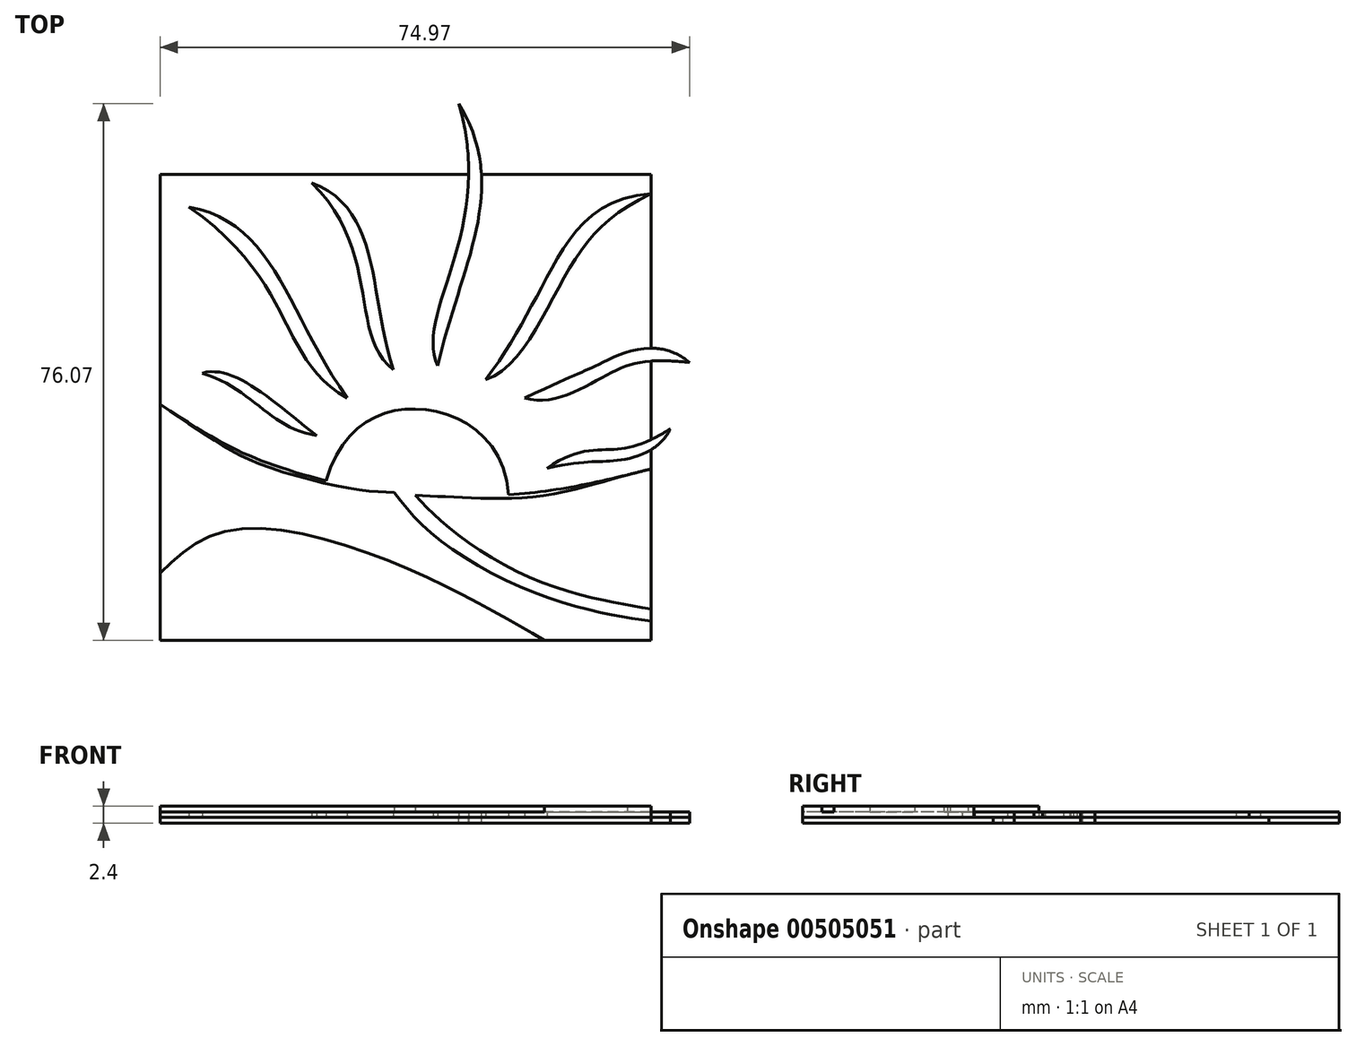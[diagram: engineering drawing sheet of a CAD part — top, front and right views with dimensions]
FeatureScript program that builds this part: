
annotation { "Feature Type Name" : "Feature", "Feature Type Description" : "" }
export const myFeature = defineFeature(function(context is Context, id is Id, definition is map)
    precondition{}
    {
        {
            var Q0;
            Q0=qCreatedBy(makeId("Top.planeOp"),FACE);
            var sketch = newSketch(context, id + "F0", { "sketchPlane" : qUnion([Q0])});
            skFitSpline(sketch, "E0", {"points": [v(7.74, 45.02) * mm, v(4.8, 7.87) * mm], "startDerivative": vector(22.58, -36) * mm, "endDerivative": vector(-9.15, -41.56) * mm});
            skFitSpline(sketch, "E1", {"points": [v(7.74, 45.02) * mm, v(4.8, 7.87) * mm], "startDerivative": vector(16.22, -53.48) * mm, "endDerivative": vector(10.7, -21.96) * mm});
            skFitSpline(sketch, "E2", {"points": [v(-13.07, 33.8) * mm, v(-1.52, 7.33) * mm], "startDerivative": vector(29.95, -11.67) * mm, "endDerivative": vector(10.67, -32.95) * mm});
            skFitSpline(sketch, "E3", {"points": [v(-13.07, 33.8) * mm, v(-1.52, 7.33) * mm], "startDerivative": vector(29.76, -29.08) * mm, "endDerivative": vector(19.1, -14.6) * mm});
            skFitSpline(sketch, "E4", {"points": [v(-30.44, 30.38) * mm, v(-8.06, 3.29) * mm], "startDerivative": vector(36.4, -6.71) * mm, "endDerivative": vector(26.15, -37.64) * mm});
            skFitSpline(sketch, "E5", {"points": [v(-30.44, 30.38) * mm, v(-8.06, 3.29) * mm], "startDerivative": vector(46.65, -33.04) * mm, "endDerivative": vector(30.4, -17.67) * mm});
            skFitSpline(sketch, "E6", {"points": [v(-28.55, 6.82) * mm, v(-12.38, -2.01) * mm], "startDerivative": vector(13.32, 3.79) * mm, "endDerivative": vector(19.77, -15.57) * mm});
            skFitSpline(sketch, "E7", {"points": [v(-28.55, 6.82) * mm, v(-12.38, -2.01) * mm], "startDerivative": vector(21.88, -6.87) * mm, "endDerivative": vector(19.77, -2.95) * mm});
            skFitSpline(sketch, "E8", {"points": [v(34.97, 32.25) * mm, v(20.43, 20.76) * mm, v(11.57, 5.91) * mm], "startDerivative": vector(-48.83, -2.88) * mm, "endDerivative": vector(-23.4, -30.3) * mm});
            skFitSpline(sketch, "E9", {"points": [v(34.97, 32.25) * mm, v(22.17, 19.45) * mm, v(11.57, 5.91) * mm], "startDerivative": vector(-41.02, -19.12) * mm, "endDerivative": vector(-28.23, -8.78) * mm});
            skFitSpline(sketch, "E10", {"points": [v(17.1, 3.33) * mm, v(27.54, 8.06) * mm, v(40.44, 8.34) * mm], "startDerivative": vector(45.36, 20.62) * mm, "endDerivative": vector(27.22, -23) * mm});
            skFitSpline(sketch, "E11", {"points": [v(17.1, 3.33) * mm, v(28.93, 6.67) * mm, v(40.44, 8.34) * mm], "startDerivative": vector(23.68, -8.22) * mm, "endDerivative": vector(37.55, -3.72) * mm});
            skFitSpline(sketch, "E12", {"points": [v(20.26, -6.67) * mm, v(29.5, -4) * mm, v(37.72, -1.06) * mm], "startDerivative": vector(23.46, 16.94) * mm, "endDerivative": vector(22.55, 14.35) * mm});
            skFitSpline(sketch, "E13", {"points": [v(20.26, -6.67) * mm, v(30.1, -5.56) * mm, v(37.72, -1.06) * mm], "startDerivative": vector(33.1, 7.46) * mm, "endDerivative": vector(9.27, 19.9) * mm});
            skFitSpline(sketch, "E14", {"points": [v(1.58, -10.48) * mm, v(16.98, -20.87) * mm, v(34.98, -26.6) * mm], "startDerivative": vector(27.12, -26.11) * mm, "endDerivative": vector(39.88, -7.31) * mm});
            skFitSpline(sketch, "E15", {"points": [v(-1.37, -10.12) * mm, v(16.48, -22.6) * mm, v(34.98, -28.32) * mm], "startDerivative": vector(30.47, -33.38) * mm, "endDerivative": vector(41.23, -6.87) * mm});
            skFitSpline(sketch, "E16", {"points": [v(1.58, -10.48) * mm, v(19.87, -9.92) * mm, v(34.98, -6.75) * mm], "startDerivative": vector(38.98, -1.92) * mm, "endDerivative": vector(30.53, 7.96) * mm});
            skFitSpline(sketch, "E17", {"points": [v(-34.53, -21.5) * mm, v(-7.42, -19.32) * mm, v(19.89, -31.05) * mm], "startDerivative": vector(55.55, 36.09) * mm, "endDerivative": vector(52.91, -30.06) * mm});
            skFitSpline(sketch, "E18", {"points": [v(-34.53, -23.76) * mm, v(-8.68, -20.91) * mm, v(16.38, -31.05) * mm], "startDerivative": vector(51.38, 35.5) * mm, "endDerivative": vector(49.5, -23.12) * mm});
            skFitSpline(sketch, "E19", {"points": [v(-34.53, 2.42) * mm, v(-18.75, -6.1) * mm, v(-1.37, -10.12) * mm], "startDerivative": vector(44.86, -30.13) * mm, "endDerivative": vector(37.4, -3.65) * mm});
            skFitSpline(sketch, "E20", {"points": [v(-11.02, -8.42) * mm, v(2.1, 1.72) * mm, v(14.8, -10.43) * mm], "startDerivative": vector(13.26, 46.27) * mm, "endDerivative": vector(3.47, -48.26) * mm});
            skLineSegment(sketch, "E21", {"start": v(-34.53, 35) * mm, "end": v(-34.53, -31.05) * mm});
            skLineSegment(sketch, "E22", {"start": v(-34.53, 35) * mm, "end": v(9.16, 35) * mm});
            skLineSegment(sketch, "E23", {"start": v(-34.53, -31.05) * mm, "end": v(34.98, -31.05) * mm});
            skLineSegment(sketch, "E24.trimOffspring", {"start": v(10.97, 35) * mm, "end": v(34.97, 35) * mm});
            skLineSegment(sketch, "E25", {"start": v(34.98, -31.05) * mm, "end": v(34.98, -4.04) * mm});
            skLineSegment(sketch, "E26.trimOffspring", {"start": v(34.98, 10.35) * mm, "end": v(34.97, 35) * mm});
            skLineSegment(sketch, "E27.trimOffspring", {"start": v(34.98, -2.6) * mm, "end": v(34.98, 8.53) * mm});
            skSolve(sketch);
        }
        {
            var Q0;
            Q0 = qSketchRegion(id + "F0", true);
            var Q1;
            Q1=makeQuery(id+"F0.imprint","IMPRINT",FACE,{"disambiguationData":[TD([[makeQuery(id+"F0.imprint","IMPRINT",EDGE,{"derivedFrom":sQuery(id+"F0.wireOp",EDGE,"E2")}),-1.0]])]});
            var Q2;
            Q2=makeQuery(id+"F0.imprint","IMPRINT",FACE,{"disambiguationData":[TD([[makeQuery(id+"F0.imprint","IMPRINT",EDGE,{"derivedFrom":sQuery(id+"F0.wireOp",EDGE,"E4")}),-1.0]])]});
            var Q3;
            Q3=makeQuery(id+"F0.imprint","IMPRINT",FACE,{"disambiguationData":[TD([[makeQuery(id+"F0.imprint","IMPRINT",EDGE,{"derivedFrom":sQuery(id+"F0.wireOp",EDGE,"E6")}),-1.0]])]});
            extrude(context, id + "F1", {"entities" : qUnion([Q0, Q1, Q2, Q3]), "oppositeDirection" : true, "depth" : .8 * mm});
        }
        {
            var Q0;
            Q0=makeQuery(id+"F0.imprint","IMPRINT",FACE,{"disambiguationData":[TD([[makeQuery(id+"F0.imprint","IMPRINT",EDGE,{"derivedFrom":sQuery(id+"F0.wireOp",EDGE,"E6")}),-1.0]])]});
            var Q1;
            Q1=makeQuery(id+"F0.imprint","IMPRINT",FACE,{"disambiguationData":[TD([[makeQuery(id+"F0.imprint","IMPRINT",EDGE,{"derivedFrom":sQuery(id+"F0.wireOp",EDGE,"E4")}),-1.0]])]});
            var Q2;
            Q2=makeQuery(id+"F0.imprint","IMPRINT",FACE,{"disambiguationData":[TD([[makeQuery(id+"F0.imprint","IMPRINT",EDGE,{"derivedFrom":sQuery(id+"F0.wireOp",EDGE,"E2")}),-1.0]])]});
            var Q3;
            Q3=makeQuery(id+"F0.imprint","IMPRINT",FACE,{"disambiguationData":[TD([[makeQuery(id+"F0.imprint","IMPRINT",EDGE,{"derivedFrom":sQuery(id+"F0.wireOp",EDGE,"E8")}),1.0]])]});
            var Q4;
            {var subQ0=sQuery(id+"F0.wireOp",EDGE,"E11");var subQ1=sQuery(id+"F0.wireOp",EDGE,"E10");var subQ2=makeQuery(id+"F0.imprint","INTERSECT",VERTEX,{"disambiguationData":[OD(0.0)],"derivedFrom":[subQ1,subQ0]});Q4=makeQuery(id+"F0.imprint","IMPRINT",FACE,{"disambiguationData":[TD([[makeQuery(id+"F0.imprint","IMPRINT",EDGE,{"disambiguationData":[TD([[subQ2,-1.0]])],"derivedFrom":subQ1}),-1.0]])]});}
            var Q5;
            {var subQ0=sQuery(id+"F0.wireOp",EDGE,"E1");var subQ1=sQuery(id+"F0.wireOp",EDGE,"E0");var subQ2=makeQuery(id+"F0.imprint","INTERSECT",VERTEX,{"disambiguationData":[OD(0.0)],"derivedFrom":[subQ1,subQ0]});Q5=makeQuery(id+"F0.imprint","IMPRINT",FACE,{"disambiguationData":[TD([[makeQuery(id+"F0.imprint","IMPRINT",EDGE,{"disambiguationData":[TD([[subQ2,-1.0]])],"derivedFrom":subQ1}),-1.0]])]});}
            var Q6;
            {var subQ0=sQuery(id+"F0.wireOp",EDGE,"E13");var subQ1=sQuery(id+"F0.wireOp",EDGE,"E12");var subQ2=makeQuery(id+"F0.imprint","INTERSECT",VERTEX,{"disambiguationData":[OD(0.0)],"derivedFrom":[subQ1,subQ0]});Q6=makeQuery(id+"F0.imprint","IMPRINT",FACE,{"disambiguationData":[TD([[makeQuery(id+"F0.imprint","IMPRINT",EDGE,{"disambiguationData":[TD([[subQ2,-1.0]])],"derivedFrom":subQ1}),-1.0]])]});}
            var Q7;
            {var subQ4=sQuery(id+"F0.wireOp",EDGE,"E14");Q7=makeQuery(id+"F0.imprint","IMPRINT",FACE,{"disambiguationData":[TD([[makeQuery(id+"F0.imprint","IMPRINT",EDGE,{"derivedFrom":subQ4}),-1.0]])]});}
            var Q8;
            {var subQ0=sQuery(id+"F0.wireOp",EDGE,"E17");Q8=makeQuery(id+"F0.imprint","IMPRINT",FACE,{"disambiguationData":[TD([[makeQuery(id+"F0.imprint","IMPRINT",EDGE,{"derivedFrom":subQ0}),-1.0]])]});}
            var Q9;
            {var subQ1=sQuery(id+"F0.wireOp",EDGE,"E15");Q9=makeQuery(id+"F0.imprint","IMPRINT",FACE,{"disambiguationData":[TD([[makeQuery(id+"F0.imprint","IMPRINT",EDGE,{"derivedFrom":subQ1}),-1.0]])]});}
            var Q10;
            {var subQ0=sQuery(id+"F0.wireOp",EDGE,"E18");Q10=makeQuery(id+"F0.imprint","IMPRINT",FACE,{"disambiguationData":[TD([[makeQuery(id+"F0.imprint","IMPRINT",EDGE,{"derivedFrom":subQ0}),-1.0]])]});}
            var Q11;
            {var subQ0=sQuery(id+"F0.wireOp",EDGE,"E14");Q11=makeQuery(id+"F0.imprint","IMPRINT",FACE,{"disambiguationData":[TD([[makeQuery(id+"F0.imprint","IMPRINT",EDGE,{"derivedFrom":subQ0}),1.0]])]});}
            extrude(context, id + "F2", {"entities" : qUnion([Q0, Q1, Q2, Q3, Q4, Q5, Q6, Q7, Q8, Q9, Q10, Q11]), "depth" : .8 * mm});
        }
        {
            var Q0;
            Q0=makeQuery(id+"F2.opExtrude","CAP_FACE",FACE,{"disambiguationData":[OSD([sQuery(id+"F0.wireOp",EDGE,"E16"),sQuery(id+"F0.wireOp",EDGE,"E19"),sQuery(id+"F0.wireOp",EDGE,"E20"),sQuery(id+"F0.wireOp",EDGE,"E21"),sQuery(id+"F0.wireOp",EDGE,"E23"),sQuery(id+"F0.wireOp",EDGE,"E25")])],"isStart":false});
            var sketch = newSketch(context, id + "F3", { "sketchPlane" : qUnion([Q0])});
            skFitSpline(sketch, "E28.0", {"points": [v(-34.53, 2.42) * mm, v(-27.04, -2.61) * mm, v(-20.2, -6.14) * mm, v(-7.6, -9.51) * mm, v(-1.37, -10.12) * mm]});
            skFitSpline(sketch, "E29.0", {"points": [v(-34.53, 2.42) * mm, v(-27.04, -2.61) * mm, v(-20.2, -6.14) * mm, v(-7.6, -9.51) * mm, v(-1.37, -10.12) * mm]});
            skLineSegment(sketch, "E30.0", {"start": v(-34.53, 35) * mm, "end": v(-34.53, -21.5) * mm});
            skFitSpline(sketch, "E31.0", {"points": [v(-34.53, -21.5) * mm, v(-25.47, -15.62) * mm, v(-6.73, -18.1) * mm, v(10.87, -25.93) * mm, v(19.89, -31.05) * mm]});
            skFitSpline(sketch, "E32.0", {"points": [v(-34.53, -23.76) * mm, v(-26.04, -17.9) * mm, v(-8.03, -19.39) * mm, v(8.05, -27.16) * mm, v(16.38, -31.05) * mm]});
            skFitSpline(sketch, "E33.0", {"points": [v(-34.53, -23.76) * mm, v(-26.04, -17.9) * mm, v(-8.03, -19.39) * mm, v(8.05, -27.16) * mm, v(16.38, -31.05) * mm]});
            skLineSegment(sketch, "E34.0", {"start": v(-34.53, -31.05) * mm, "end": v(16.38, -31.05) * mm});
            skFitSpline(sketch, "E35.0", {"points": [v(-1.37, -10.12) * mm, v(3.85, -15.85) * mm, v(16.16, -23.33) * mm, v(28.3, -27.21) * mm, v(34.98, -28.32) * mm]});
            skFitSpline(sketch, "E36.0", {"points": [v(1.58, -10.48) * mm, v(6.08, -14.81) * mm, v(16.86, -21.7) * mm, v(28.3, -25.38) * mm, v(34.98, -26.6) * mm]});
            skFitSpline(sketch, "E37.0", {"points": [v(1.58, -10.48) * mm, v(8.35, -10.81) * mm, v(19.59, -10.55) * mm, v(30.1, -8.02) * mm, v(34.98, -6.75) * mm]});
            skLineSegment(sketch, "E38.0", {"start": v(34.98, -31.05) * mm, "end": v(34.98, -28.32) * mm});
            skLineSegment(sketch, "E39.trimOffspring", {"start": v(19.89, -31.05) * mm, "end": v(34.98, -31.05) * mm});
            skLineSegment(sketch, "E40.trimOffspring", {"start": v(34.98, -26.6) * mm, "end": v(34.98, -4.04) * mm});
            skLineSegment(sketch, "E41.trimOffspring", {"start": v(-34.53, -23.76) * mm, "end": v(-34.53, -31.05) * mm});
            skSolve(sketch);
        }
        {
            var Q0;
            Q0=makeQuery(id+"F3.imprint","IMPRINT",FACE,{"disambiguationData":[TD([[makeQuery(id+"F3.imprint","IMPRINT",EDGE,{"derivedFrom":sQuery(id+"F3.wireOp",EDGE,"E33.0")}),-1.0]])]});
            var Q1;
            {var subQ0=sQuery(id+"F3.wireOp",EDGE,"E31.0");Q1=makeQuery(id+"F3.imprint","IMPRINT",FACE,{"disambiguationData":[TD([[makeQuery(id+"F3.imprint","IMPRINT",EDGE,{"derivedFrom":subQ0}),1.0]])]});}
            var Q2;
            {var subQ0=sQuery(id+"F3.wireOp",EDGE,"E36.0");Q2=makeQuery(id+"F3.imprint","IMPRINT",FACE,{"disambiguationData":[TD([[makeQuery(id+"F3.imprint","IMPRINT",EDGE,{"derivedFrom":subQ0}),1.0]])]});}
            extrude(context, id + "F4", {"entities" : qUnion([Q0, Q1, Q2]), "operationType" : NewBodyOperationType.ADD, "depth" : .8 * mm});
        }
    });
